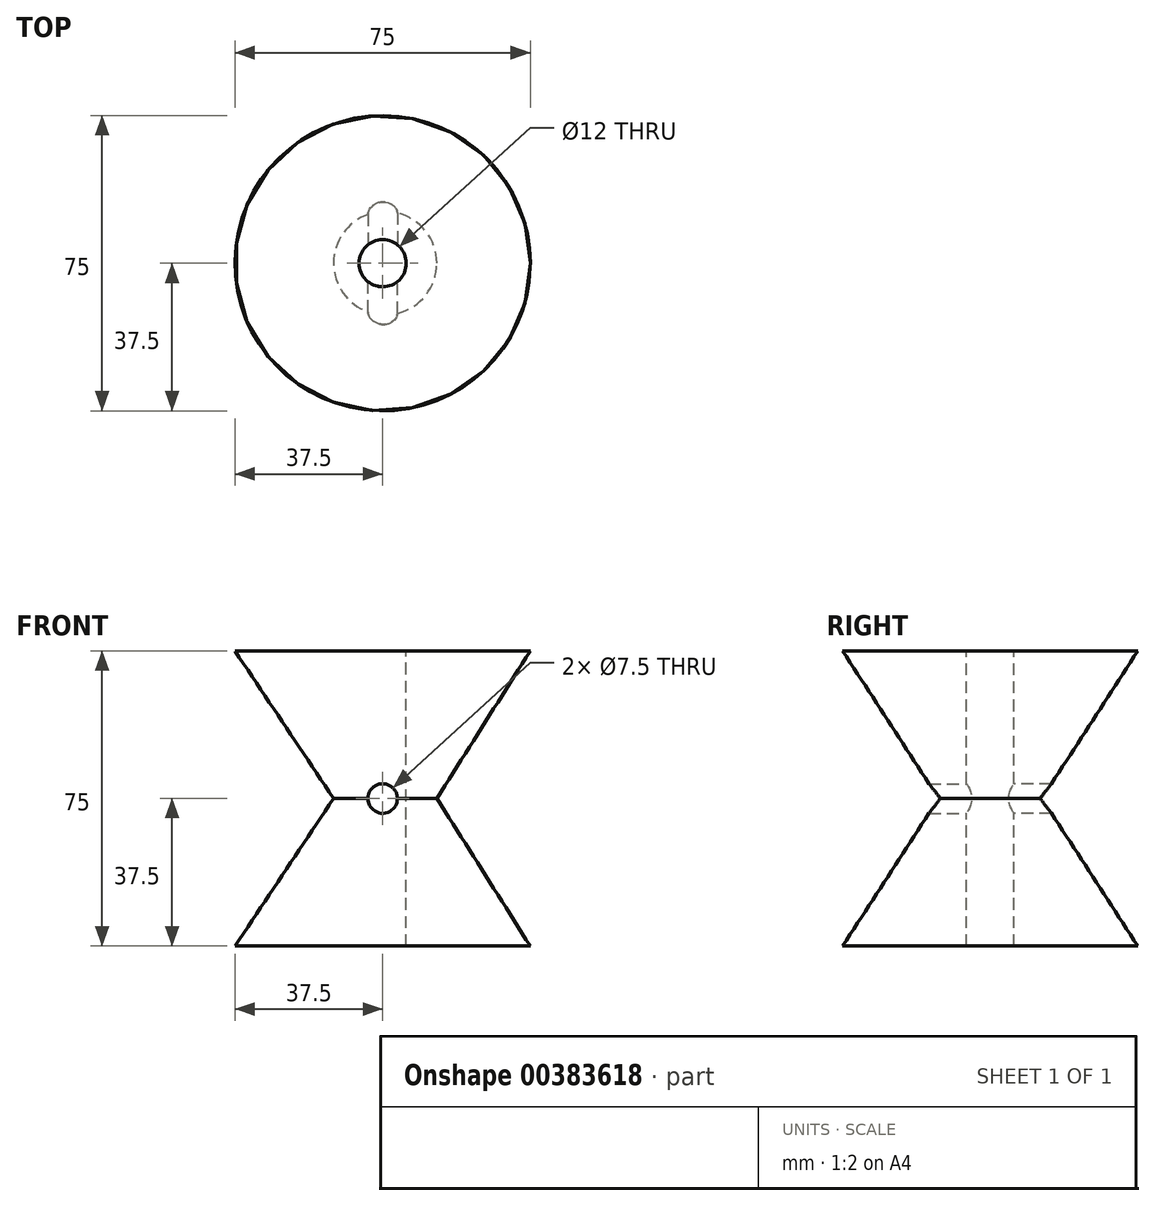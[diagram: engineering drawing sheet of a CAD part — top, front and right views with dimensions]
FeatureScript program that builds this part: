
annotation { "Feature Type Name" : "Feature", "Feature Type Description" : "" }
export const myFeature = defineFeature(function(context is Context, id is Id, definition is map)
    precondition{}
    {
        {
            var Q0;
            Q0=qCreatedBy(makeId("Top.planeOp"),FACE);
            var sketch = newSketch(context, id + "F0", { "sketchPlane" : qUnion([Q0])});
            skCircle(sketch, "E0", {"center": v(0, 0) * mm, "radius": 37.5 * mm});
            skSolve(sketch);
        }
        {
            var Q0;
            Q0=qCreatedBy(makeId("Top.planeOp"),FACE);
            cPlane(context, id + "F1", {"entities" : qUnion([Q0]), "cplaneType" : CPlaneType.OFFSET, "offset" : 37.5 * mm, "width" : 150 * mm, "height" : 150 * mm});
        }
        {
            var Q0;
            Q0=qCreatedBy(id+"F1.planeOp",FACE);
            var sketch = newSketch(context, id + "F2", { "sketchPlane" : qUnion([Q0])});
            skCircle(sketch, "E1", {"center": v(0.64, 0) * mm, "radius": 13.12 * mm});
            skSolve(sketch);
        }
        {
            var Q0;
            Q0=makeQuery(id+"F0.imprint","IMPRINT",FACE,{"disambiguationData":[TD([[makeQuery(id+"F0.imprint","IMPRINT",EDGE,{"derivedFrom":sQuery(id+"F0.wireOp",EDGE,"E0")}),1.0]])]});
            var Q1;
            Q1=makeQuery(id+"F2.imprint","IMPRINT",FACE,{"disambiguationData":[TD([[makeQuery(id+"F2.imprint","IMPRINT",EDGE,{"derivedFrom":sQuery(id+"F2.wireOp",EDGE,"E1")}),1.0]])]});
            loft(context, id + "F3", {"sheetProfilesArray" : [{ "sheetProfileEntities" : qUnion([Q0]) }, { "sheetProfileEntities" : qUnion([Q1]) }]});
        }
        {
            var Q0;
            Q0=makeQuery(id+"F3.opLoft","SWEPT_BODY",BODY,{"disambiguationData":[OSD([makeQuery(id+"F0.imprint","IMPRINT",FACE,{"disambiguationData":[TD([[makeQuery(id+"F0.imprint","IMPRINT",EDGE,{"derivedFrom":sQuery(id+"F0.wireOp",EDGE,"E0")}),1.0]])]}),makeQuery(id+"F2.imprint","IMPRINT",FACE,{"disambiguationData":[TD([[makeQuery(id+"F2.imprint","IMPRINT",EDGE,{"derivedFrom":sQuery(id+"F2.wireOp",EDGE,"E1")}),1.0]])]})])]});
            var Q1;
            Q1=qCreatedBy(id+"F1.planeOp",FACE);
            mirror(context, id + "F4", {"operationType" : NewBodyOperationType.ADD, "entities" : qUnion([Q0]), "mirrorPlane" : qUnion([Q1])});
        }
        {
            var Q0;
            Q0=makeQuery(id+"F4.opPattern","COPY",FACE,{"derivedFrom":makeQuery(id+"F3.opLoft","CAP_FACE",FACE,{"disambiguationData":[OSD([makeQuery(id+"F0.imprint","IMPRINT",FACE,{"disambiguationData":[TD([[makeQuery(id+"F0.imprint","IMPRINT",EDGE,{"derivedFrom":sQuery(id+"F0.wireOp",EDGE,"E0")}),1.0]])]})])],"isStart":true}),"instanceName":"1"});
            var sketch = newSketch(context, id + "F5", { "sketchPlane" : qUnion([Q0])});
            skCircle(sketch, "E2", {"center": v(0, 0) * mm, "radius": 6 * mm});
            skSolve(sketch);
        }
        {
            var Q0;
            Q0=makeQuery(id+"F5.imprint","IMPRINT",FACE,{"disambiguationData":[TD([[makeQuery(id+"F5.imprint","IMPRINT",EDGE,{"derivedFrom":sQuery(id+"F5.wireOp",EDGE,"E2")}),1.0]])]});
            extrude(context, id + "F6", {"entities" : qUnion([Q0]), "operationType" : NewBodyOperationType.REMOVE, "endBound" : BoundingType.THROUGH_ALL, "oppositeDirection" : true, "depth" : 25 * mm, "offsetDistance" : 25 * mm});
        }
        {
            var Q0;
            Q0=qCreatedBy(makeId("Front.planeOp"),FACE);
            var sketch = newSketch(context, id + "F7", { "sketchPlane" : qUnion([Q0])});
            skFitSpline(sketch, "E3.0", {"points": [v(18.36, 50) * mm, v(6.7, 50) * mm, v(-4.98, 50) * mm, v(-16.64, 50) * mm], "construction": true});
            skPoint(sketch, "E4.0", {"position": v(0, 0) * mm});
            skLineSegment(sketch, "E5", {"start": v(0, 0) * mm, "end": v(0, 179.16) * mm, "construction": true});
            skPoint(sketch, "E6", {"position": v(0, 37.5) * mm});
            skCircle(sketch, "E7", {"center": v(0, 37.5) * mm, "radius": 3.75 * mm});
            skSolve(sketch);
        }
        {
            var Q0;
            Q0 = qSketchRegion(id + "F7", true);
            extrude(context, id + "F8", {"entities" : qUnion([Q0]), "operationType" : NewBodyOperationType.REMOVE, "endBound" : BoundingType.THROUGH_ALL, "oppositeDirection" : true, "depth" : 25 * mm, "offsetDistance" : 25 * mm});
        }
        {
            var Q0;
            Q0 = qSketchRegion(id + "F7", true);
            extrude(context, id + "F9", {"entities" : qUnion([Q0]), "operationType" : NewBodyOperationType.REMOVE, "endBound" : BoundingType.THROUGH_ALL, "depth" : 25 * mm, "offsetDistance" : 25 * mm});
        }
    });
